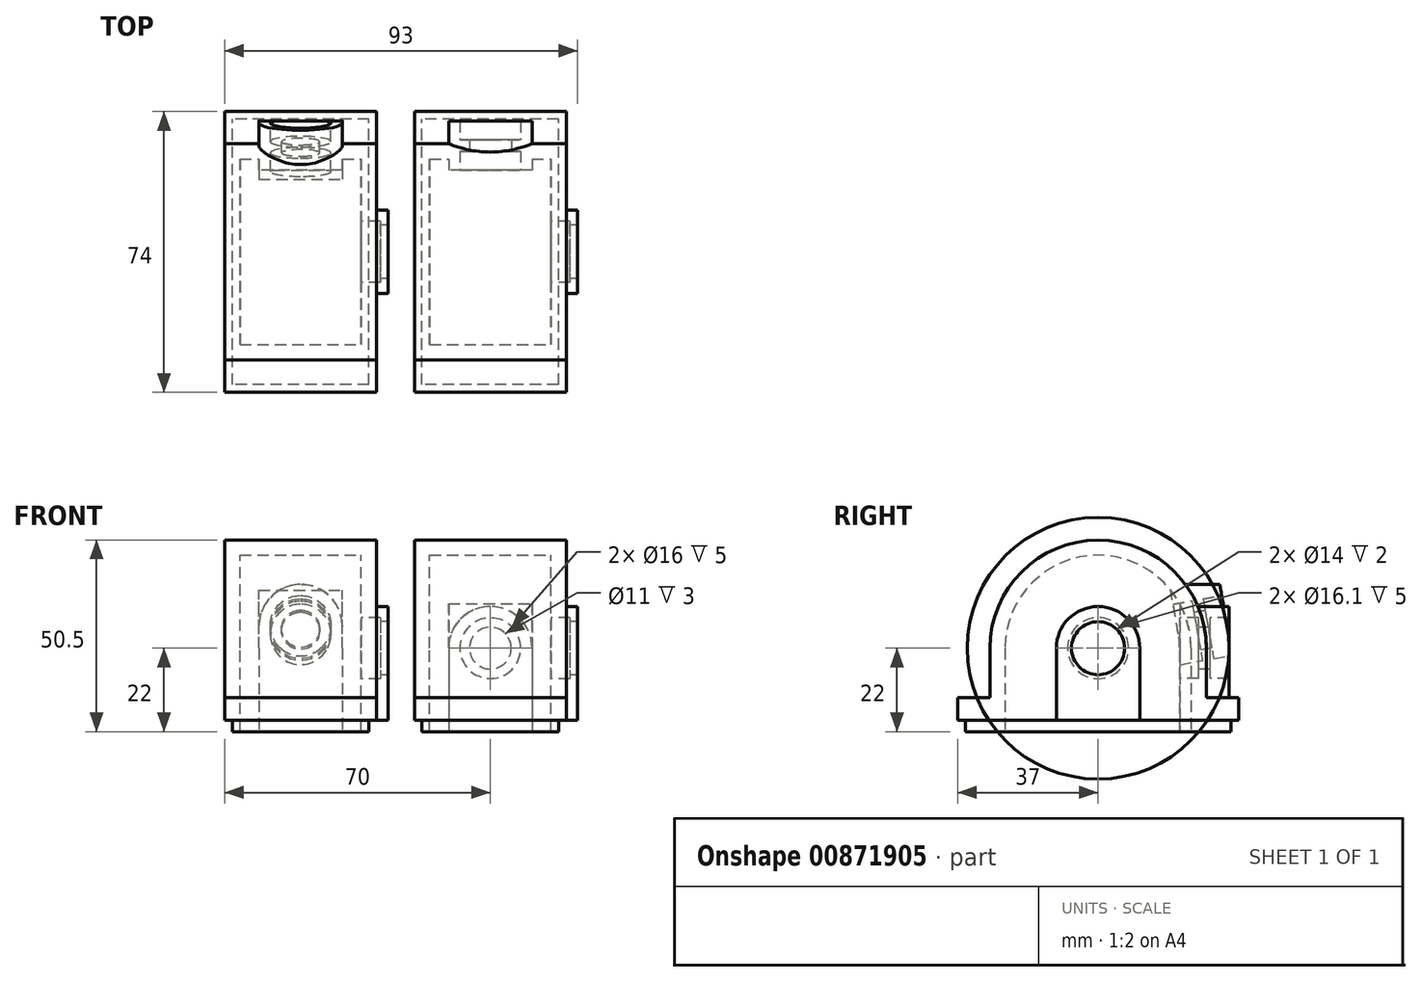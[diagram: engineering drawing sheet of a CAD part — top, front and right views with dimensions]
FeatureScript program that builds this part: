
annotation { "Feature Type Name" : "Feature", "Feature Type Description" : "" }
export const myFeature = defineFeature(function(context is Context, id is Id, definition is map)
    precondition{}
    {
        {
            var Q0;
            Q0=qCreatedBy(makeId("Right.planeOp"),FACE);
            var sketch = newSketch(context, id + "F0", { "sketchPlane" : qUnion([Q0])});
            skArc(sketch, "E0", {"start": v(28.5, 22) * mm, "mid": v(0, 50.5) * mm, "end": v(-28.5, 22) * mm});
            skLineSegment(sketch, "E1", {"start": v(-28.5, 22) * mm, "end": v(28.5, 22) * mm, "construction": true});
            skLineSegment(sketch, "E2", {"start": v(-28.5, 22) * mm, "end": v(-28.5, 9) * mm});
            skLineSegment(sketch, "E3", {"start": v(28.5, 22) * mm, "end": v(28.5, 9) * mm});
            skLineSegment(sketch, "E4.top", {"start": v(37, 9) * mm, "end": v(28.5, 9) * mm});
            skLineSegment(sketch, "E4.left", {"start": v(37, 0) * mm, "end": v(37, 9) * mm});
            skLineSegment(sketch, "E4.right", {"start": v(-37, 0) * mm, "end": v(-37, 9) * mm});
            skPoint(sketch, "E4.middle", {"position": v(0, 4.5) * mm});
            skLineSegment(sketch, "E5.trimOffspring", {"start": v(-28.5, 9) * mm, "end": v(-37, 9) * mm});
            skLineSegment(sketch, "E6", {"start": v(-37, 0) * mm, "end": v(37, 0) * mm});
            skSolve(sketch);
        }
        {
            var Q0;
            Q0=qSketchRegion(id+"F0",true);
            extrude(context, id + "F1", {"entities" : qUnion([Q0]), "depth" : 40 * mm, "offsetDistance" : 25 * mm, "symmetric" : true});
        }
        {
            var Q0;
            Q0=qCreatedBy(makeId("Right.planeOp"),FACE);
            var sketch = newSketch(context, id + "F2", { "sketchPlane" : qUnion([Q0])});
            skArc(sketch, "E7", {"start": v(24.5, 22) * mm, "mid": v(0, 46.5) * mm, "end": v(-24.5, 22) * mm});
            skLineSegment(sketch, "E8", {"start": v(-24.5, 22) * mm, "end": v(24.5, 22) * mm, "construction": true});
            skLineSegment(sketch, "E9", {"start": v(-24.5, 22) * mm, "end": v(-24.5, 0) * mm});
            skLineSegment(sketch, "E10", {"start": v(-24.5, 0) * mm, "end": v(24.5, 0) * mm});
            skLineSegment(sketch, "E11", {"start": v(24.5, 0) * mm, "end": v(24.5, 22) * mm});
            skSolve(sketch);
        }
        {
            var Q0;
            Q0=qSketchRegion(id+"F2",true);
            extrude(context, id + "F3", {"entities" : qUnion([Q0]), "operationType" : NewBodyOperationType.REMOVE, "oppositeDirection" : true, "depth" : 32 * mm, "offsetDistance" : 25 * mm, "symmetric" : true});
        }
        {
            var Q0;
            Q0=makeQuery(id+"F1.opExtrude","CAP_FACE",FACE,{"disambiguationData":[OSD([sQuery(id+"F0.wireOp",EDGE,"E0"),sQuery(id+"F0.wireOp",EDGE,"E2"),sQuery(id+"F0.wireOp",EDGE,"E3"),sQuery(id+"F0.wireOp",EDGE,"E4.top"),sQuery(id+"F0.wireOp",EDGE,"E4.left"),sQuery(id+"F0.wireOp",EDGE,"E4.right"),sQuery(id+"F0.wireOp",EDGE,"E5.trimOffspring"),sQuery(id+"F0.wireOp",EDGE,"E6")])],"isStart":false});
            var sketch = newSketch(context, id + "F4", { "sketchPlane" : qUnion([Q0])});
            skArc(sketch, "E12", {"start": v(11, 22) * mm, "mid": v(0, 33) * mm, "end": v(-11, 22) * mm});
            skLineSegment(sketch, "E13", {"start": v(-11, 22) * mm, "end": v(-11, 0) * mm});
            skLineSegment(sketch, "E14", {"start": v(-11, 0) * mm, "end": v(11, 0) * mm});
            skLineSegment(sketch, "E15", {"start": v(11, 0) * mm, "end": v(11, 22) * mm});
            skSolve(sketch);
        }
        {
            var Q0;
            Q0=qSketchRegion(id+"F4",true);
            extrude(context, id + "F5", {"entities" : qUnion([Q0]), "operationType" : NewBodyOperationType.ADD, "depth" : 3 * mm, "offsetDistance" : 25 * mm});
        }
        {
            var Q0;
            Q0=qCreatedBy(makeId("Front.planeOp"),FACE);
            var sketch = newSketch(context, id + "F6", { "sketchPlane" : qUnion([Q0])});
            skLineSegment(sketch, "E16", {"start": v(42.03, 22) * mm, "end": v(7.34, 22) * mm, "construction": true});
            skLineSegment(sketch, "E17", {"start": v(16, 22) * mm, "end": v(16, 30.05) * mm});
            skLineSegment(sketch, "E18", {"start": v(16, 30.05) * mm, "end": v(21, 30.05) * mm});
            skLineSegment(sketch, "E19", {"start": v(21, 30.05) * mm, "end": v(21, 29) * mm});
            skLineSegment(sketch, "E20", {"start": v(21, 29) * mm, "end": v(23, 29) * mm});
            skLineSegment(sketch, "E21", {"start": v(23, 29) * mm, "end": v(23, 22) * mm});
            skLineSegment(sketch, "E22", {"start": v(23, 22) * mm, "end": v(16, 22) * mm});
            skLineSegment(sketch, "E23", {"start": v(16, 22) * mm, "end": v(23, 22) * mm});
            skSolve(sketch);
        }
        {
            var Q0;
            Q0=qSketchRegion(id+"F6",true);
            var Q1;
            Q1=sQuery(id+"F6.wireOp",EDGE,"E16");
            revolve(context, id + "F7", {"operationType" : NewBodyOperationType.REMOVE, "surfaceOperationType" : NewSurfaceOperationType.NEW, "entities" : qUnion([Q0]), "axis" : qUnion([Q1]), "revolveType" : RevolveType.FULL, "oppositeDirection" : true});
        }
        {
            var Q0;
            {var subQ0=sQuery(id+"F4.wireOp",EDGE,"E14");Q0=makeQuery(id+"Fj3ByAB7jm97h4G_1.1.F5.boolean.opBoolean","MERGE",FACE,{"derivedFrom":[makeQuery(id+"F5.boolean.opBoolean","MERGE",FACE,{"derivedFrom":[makeQuery(id+"F1.opExtrude","SWEPT_FACE",FACE,{"disambiguationData":[OSD([sQuery(id+"F0.wireOp",EDGE,"E6")])]}),makeQuery(id+"F5.opExtrude","SWEPT_FACE",FACE,{"disambiguationData":[OSD([subQ0])]})]}),makeQuery(id+"Fj3ByAB7jm97h4G_1.1.F5.opExtrude","SWEPT_FACE",FACE,{"disambiguationData":[OSD([subQ0])]})]});}
            var sketch = newSketch(context, id + "F8", { "sketchPlane" : qUnion([Q0])});
            skLineSegment(sketch, "E24.bottom", {"start": v(18, 35) * mm, "end": v(-18, 35) * mm});
            skLineSegment(sketch, "E24.top", {"start": v(18, -35) * mm, "end": v(-18, -35) * mm});
            skLineSegment(sketch, "E24.left", {"start": v(18, 35) * mm, "end": v(18, -35) * mm});
            skLineSegment(sketch, "E24.right", {"start": v(-18, 35) * mm, "end": v(-18, -35) * mm});
            skPoint(sketch, "E24.middle", {"position": v(0, 0) * mm});
            skLineSegment(sketch, "E25.0.0", {"start": v(-20, 37) * mm, "end": v(-20, 11) * mm});
            skLineSegment(sketch, "E25.0.1", {"start": v(-20, 11) * mm, "end": v(-23, 11) * mm});
            skLineSegment(sketch, "E25.0.2", {"start": v(-23, 11) * mm, "end": v(-23, -11) * mm});
            skLineSegment(sketch, "E25.0.3", {"start": v(-23, -11) * mm, "end": v(-20, -11) * mm});
            skLineSegment(sketch, "E25.0.4", {"start": v(-20, -11) * mm, "end": v(-20, -37) * mm});
            skLineSegment(sketch, "E25.0.5", {"start": v(-20, -37) * mm, "end": v(20, -37) * mm});
            skLineSegment(sketch, "E25.0.6", {"start": v(20, -37) * mm, "end": v(20, -11) * mm});
            skLineSegment(sketch, "E25.0.7", {"start": v(20, -11) * mm, "end": v(23, -11) * mm});
            skLineSegment(sketch, "E25.0.8", {"start": v(23, -11) * mm, "end": v(23, 11) * mm});
            skLineSegment(sketch, "E25.0.9", {"start": v(23, 11) * mm, "end": v(20, 11) * mm});
            skLineSegment(sketch, "E25.0.10", {"start": v(20, 11) * mm, "end": v(20, 37) * mm});
            skLineSegment(sketch, "E25.0.11", {"start": v(20, 37) * mm, "end": v(-20, 37) * mm});
            skSolve(sketch);
        }
        {
            var Q0;
            Q0=qSketchRegion(id+"F8",true);
            extrude(context, id + "F9", {"entities" : qUnion([Q0]), "operationType" : NewBodyOperationType.REMOVE, "oppositeDirection" : true, "depth" : 3 * mm, "offsetDistance" : 25 * mm});
        }
        {
            var Q0;
            Q0=makeQuery(id+"F1.opExtrude","SWEPT_BODY",BODY,{"disambiguationData":[OSD([sQuery(id+"F0.wireOp",EDGE,"E0"),sQuery(id+"F0.wireOp",EDGE,"E2"),sQuery(id+"F0.wireOp",EDGE,"E3"),sQuery(id+"F0.wireOp",EDGE,"E4.top"),sQuery(id+"F0.wireOp",EDGE,"E4.left"),sQuery(id+"F0.wireOp",EDGE,"E4.right"),sQuery(id+"F0.wireOp",EDGE,"E5.trimOffspring"),sQuery(id+"F0.wireOp",EDGE,"E6")])]});
            transform(context, id + "F10", {"entities" : qUnion([Q0]), "transformType" : TransformType.TRANSLATION_3D, "dx" : 50 * mm, "dy" : 0 * mm, "dz" : 0 * mm, "makeCopy" : true});
        }
        {
            var Q0;
            Q0=makeQuery(id+"F10.opPattern","COPY",FACE,{"derivedFrom":makeQuery(id+"F1.opExtrude","CAP_FACE",FACE,{"disambiguationData":[OSD([sQuery(id+"F0.wireOp",EDGE,"E0"),sQuery(id+"F0.wireOp",EDGE,"E2"),sQuery(id+"F0.wireOp",EDGE,"E3"),sQuery(id+"F0.wireOp",EDGE,"E4.top"),sQuery(id+"F0.wireOp",EDGE,"E4.left"),sQuery(id+"F0.wireOp",EDGE,"E4.right"),sQuery(id+"F0.wireOp",EDGE,"E5.trimOffspring"),sQuery(id+"F0.wireOp",EDGE,"E6")])],"isStart":false}),"instanceName":"1"});
            var Q1;
            Q1=makeQuery(id+"F10.opPattern","COPY",FACE,{"derivedFrom":makeQuery(id+"F1.opExtrude","CAP_FACE",FACE,{"disambiguationData":[OSD([sQuery(id+"F0.wireOp",EDGE,"E0"),sQuery(id+"F0.wireOp",EDGE,"E2"),sQuery(id+"F0.wireOp",EDGE,"E3"),sQuery(id+"F0.wireOp",EDGE,"E4.top"),sQuery(id+"F0.wireOp",EDGE,"E4.left"),sQuery(id+"F0.wireOp",EDGE,"E4.right"),sQuery(id+"F0.wireOp",EDGE,"E5.trimOffspring"),sQuery(id+"F0.wireOp",EDGE,"E6")])],"isStart":true}),"instanceName":"1"});
            cPlane(context, id + "F11", {"entities" : qUnion([Q0, Q1]), "cplaneType" : CPlaneType.MID_PLANE, "offset" : 25 * mm, "width" : 150 * mm, "height" : 150 * mm});
        }
        {
            var Q0;
            Q0=qCreatedBy(id+"F11.planeOp",FACE);
            var sketch = newSketch(context, id + "F12", { "sketchPlane" : qUnion([Q0])});
            skLineSegment(sketch, "E26", {"start": v(21.5, 0) * mm, "end": v(21.5, 33) * mm});
            skLineSegment(sketch, "E27", {"start": v(24.84, 33) * mm, "end": v(34.5, 33) * mm});
            skLineSegment(sketch, "E28", {"start": v(34.5, 33) * mm, "end": v(34.5, 0) * mm});
            skLineSegment(sketch, "E29", {"start": v(34.5, 0) * mm, "end": v(21.5, 0) * mm});
            skLineSegment(sketch, "E30", {"start": v(24.84, 33) * mm, "end": v(21.5, 34) * mm});
            skLineSegment(sketch, "E31", {"start": v(21.5, 34) * mm, "end": v(21.5, 33) * mm});
            skSolve(sketch);
        }
        {
            var Q0;
            Q0=qSketchRegion(id+"F12",true);
            extrude(context, id + "F13", {"entities" : qUnion([Q0]), "operationType" : NewBodyOperationType.ADD, "depth" : 22 * mm, "offsetDistance" : 25 * mm, "symmetric" : true});
        }
        {
            var Q0;
            {var subQ1=sQuery(id+"F12.wireOp",EDGE,"E27");Q0=makeQuery(id+"F13.boolean.opBoolean","SPLIT",EDGE,{"disambiguationData":[TD([makeQuery(id+"F10.opPattern","COPY",FACE,{"derivedFrom":makeQuery(id+"F1.opExtrude","SWEPT_FACE",FACE,{"disambiguationData":[OSD([sQuery(id+"F0.wireOp",EDGE,"E0")])]}),"instanceName":"1"})])],"derivedFrom":makeQuery(id+"F13.opExtrude","CAP_EDGE",EDGE,{"disambiguationData":[OSD([subQ1])],"isStart":false})});}
            var Q1;
            {var subQ1=sQuery(id+"F12.wireOp",EDGE,"E27");Q1=makeQuery(id+"F13.boolean.opBoolean","SPLIT",EDGE,{"disambiguationData":[TD([makeQuery(id+"F10.opPattern","COPY",FACE,{"derivedFrom":makeQuery(id+"F1.opExtrude","SWEPT_FACE",FACE,{"disambiguationData":[OSD([sQuery(id+"F0.wireOp",EDGE,"E0")])]}),"instanceName":"1"})])],"derivedFrom":makeQuery(id+"F13.opExtrude","CAP_EDGE",EDGE,{"disambiguationData":[OSD([subQ1])],"isStart":true})});}
            fillet(context, id + "F14", {"entities" : qUnion([Q0, Q1]), "radius" : 11 * mm, "tangentPropagation" : true, "allowEdgeOverflow" : false});
        }
        {
            var Q0;
            Q0=qCreatedBy(id+"F11.planeOp",FACE);
            var sketch = newSketch(context, id + "F15", { "sketchPlane" : qUnion([Q0])});
            skCircle(sketch, "E32.0", {"center": v(0, 22) * mm, "radius": 7 * mm, "construction": true});
            skLineSegment(sketch, "E33", {"start": v(0, 22) * mm, "end": v(49.84, 22) * mm, "construction": true});
            skLineSegment(sketch, "E34", {"start": v(21.5, 22) * mm, "end": v(21.5, 30) * mm});
            skLineSegment(sketch, "E35", {"start": v(21.5, 30) * mm, "end": v(26.5, 30) * mm});
            skLineSegment(sketch, "E36", {"start": v(26.5, 30) * mm, "end": v(26.5, 27.5) * mm});
            skLineSegment(sketch, "E37", {"start": v(26.5, 27.5) * mm, "end": v(29.5, 27.5) * mm});
            skLineSegment(sketch, "E38", {"start": v(29.5, 27.5) * mm, "end": v(29.5, 30) * mm});
            skLineSegment(sketch, "E39", {"start": v(29.5, 30) * mm, "end": v(34.5, 30) * mm});
            skLineSegment(sketch, "E40", {"start": v(34.5, 30) * mm, "end": v(34.5, 22) * mm});
            skLineSegment(sketch, "E41.0", {"start": v(34.5, 22) * mm, "end": v(34.5, 33) * mm, "construction": true});
            skLineSegment(sketch, "E42.0", {"start": v(21.5, 0) * mm, "end": v(21.5, 0) * mm});
            skLineSegment(sketch, "E43", {"start": v(21.5, 22) * mm, "end": v(34.5, 22) * mm});
            skSolve(sketch);
        }
        {
            var Q0;
            Q0=qSketchRegion(id+"F15",true);
            var Q1;
            Q1=sQuery(id+"F15.wireOp",EDGE,"E33");
            revolve(context, id + "F16", {"operationType" : NewBodyOperationType.REMOVE, "surfaceOperationType" : NewSurfaceOperationType.NEW, "entities" : qUnion([Q0]), "axis" : qUnion([Q1]), "revolveType" : RevolveType.FULL});
        }
        {
            var Q0;
            Q0=qCreatedBy(makeId("Right.planeOp"),FACE);
            var sketch = newSketch(context, id + "F17", { "sketchPlane" : qUnion([Q0])});
            skCircle(sketch, "E44.0", {"center": v(0, 22) * mm, "radius": 7 * mm, "construction": true});
            skLineSegment(sketch, "E45", {"start": v(0, 22) * mm, "end": v(36.47, 22) * mm, "construction": true});
            skLineSegment(sketch, "E46", {"start": v(0, 22) * mm, "end": v(42.78, 29.54) * mm, "construction": true});
            skLineSegment(sketch, "E47", {"start": v(21.5, 0) * mm, "end": v(21.5, 22) * mm});
            skLineSegment(sketch, "E48", {"start": v(34.5, 0) * mm, "end": v(34.5, 22) * mm});
            skArc(sketch, "E49", {"start": v(21.5, 22) * mm, "mid": v(21.42, 23.87) * mm, "end": v(21.17, 25.73) * mm});
            skArc(sketch, "E50", {"start": v(34.5, 22) * mm, "mid": v(34.37, 25) * mm, "end": v(33.98, 28) * mm});
            skLineSegment(sketch, "E51", {"start": v(32.07, 38.82) * mm, "end": v(16.28, 36.04) * mm, "construction": true});
            skLineSegment(sketch, "E52", {"start": v(33.98, 28) * mm, "end": v(32.07, 38.82) * mm});
            skLineSegment(sketch, "E53", {"start": v(0, 22) * mm, "end": v(0, 50.5) * mm, "construction": true});
            skLineSegment(sketch, "E54", {"start": v(21.5, 0) * mm, "end": v(34.5, 0) * mm});
            skLineSegment(sketch, "E55", {"start": v(32.07, 38.82) * mm, "end": v(18.87, 38.82) * mm});
            skLineSegment(sketch, "E56", {"start": v(21.17, 25.73) * mm, "end": v(18.87, 38.82) * mm});
            skPoint(sketch, "E57.orphan", {"position": v(0, 38.82) * mm});
            skSolve(sketch);
        }
        {
            var Q0;
            Q0=makeQuery(id+"F17.imprint","IMPRINT",FACE,{"disambiguationData":[TD([[makeQuery(id+"F17.imprint","IMPRINT",EDGE,{"derivedFrom":sQuery(id+"F17.wireOp",EDGE,"E47")}),-1.0]])]});
            extrude(context, id + "F18", {"entities" : qUnion([Q0]), "operationType" : NewBodyOperationType.ADD, "depth" : 22 * mm, "offsetDistance" : 25 * mm, "symmetric" : true});
        }
        {
            var Q0;
            Q0=qCreatedBy(makeId("Right.planeOp"),FACE);
            var sketch = newSketch(context, id + "F19", { "sketchPlane" : qUnion([Q0])});
            skLineSegment(sketch, "E58.0", {"start": v(0, 22) * mm, "end": v(42.78, 29.54) * mm, "construction": true});
            skLineSegment(sketch, "E59.0", {"start": v(33.98, 28) * mm, "end": v(32.07, 38.82) * mm, "construction": true});
            skLineSegment(sketch, "E60", {"start": v(28.18, 32.05) * mm, "end": v(27.66, 35) * mm});
            skLineSegment(sketch, "E61", {"start": v(27.66, 35) * mm, "end": v(32.59, 35.87) * mm});
            skLineSegment(sketch, "E62", {"start": v(32.59, 35.87) * mm, "end": v(33.98, 28) * mm});
            skLineSegment(sketch, "E63", {"start": v(21.17, 25.73) * mm, "end": v(33.98, 28) * mm});
            skLineSegment(sketch, "E64", {"start": v(24.7, 34.48) * mm, "end": v(25.23, 31.53) * mm});
            skLineSegment(sketch, "E65", {"start": v(25.23, 31.53) * mm, "end": v(28.18, 32.05) * mm});
            skLineSegment(sketch, "E66", {"start": v(24.7, 34.48) * mm, "end": v(19.78, 33.61) * mm});
            skLineSegment(sketch, "E67", {"start": v(19.78, 33.61) * mm, "end": v(21.17, 25.73) * mm, "construction": true});
            skLineSegment(sketch, "E68", {"start": v(19.78, 33.61) * mm, "end": v(16.83, 33.1) * mm});
            skLineSegment(sketch, "E69", {"start": v(16.83, 33.1) * mm, "end": v(18.22, 25.21) * mm});
            skLineSegment(sketch, "E70", {"start": v(18.22, 25.21) * mm, "end": v(21.17, 25.73) * mm});
            skSolve(sketch);
        }
        {
            var Q0;
            Q0=qSketchRegion(id+"F19",true);
            var Q1;
            Q1=sQuery(id+"F19.wireOp",EDGE,"E58.0");
            revolve(context, id + "F20", {"operationType" : NewBodyOperationType.REMOVE, "surfaceOperationType" : NewSurfaceOperationType.NEW, "entities" : qUnion([Q0]), "axis" : qUnion([Q1]), "revolveType" : RevolveType.FULL, "oppositeDirection" : true});
        }
        {
            var Q0;
            Q0=makeQuery(id+"F18.opExtrude","CAP_EDGE",EDGE,{"disambiguationData":[OSD([sQuery(id+"F17.wireOp",EDGE,"E55")])],"isStart":true});
            var Q1;
            Q1=makeQuery(id+"F18.opExtrude","CAP_EDGE",EDGE,{"disambiguationData":[OSD([sQuery(id+"F17.wireOp",EDGE,"E55")])],"isStart":false});
            fillet(context, id + "F21", {"entities" : qUnion([Q0, Q1]), "radius" : 11 * mm, "tangentPropagation" : true, "allowEdgeOverflow" : false});
        }
    });
